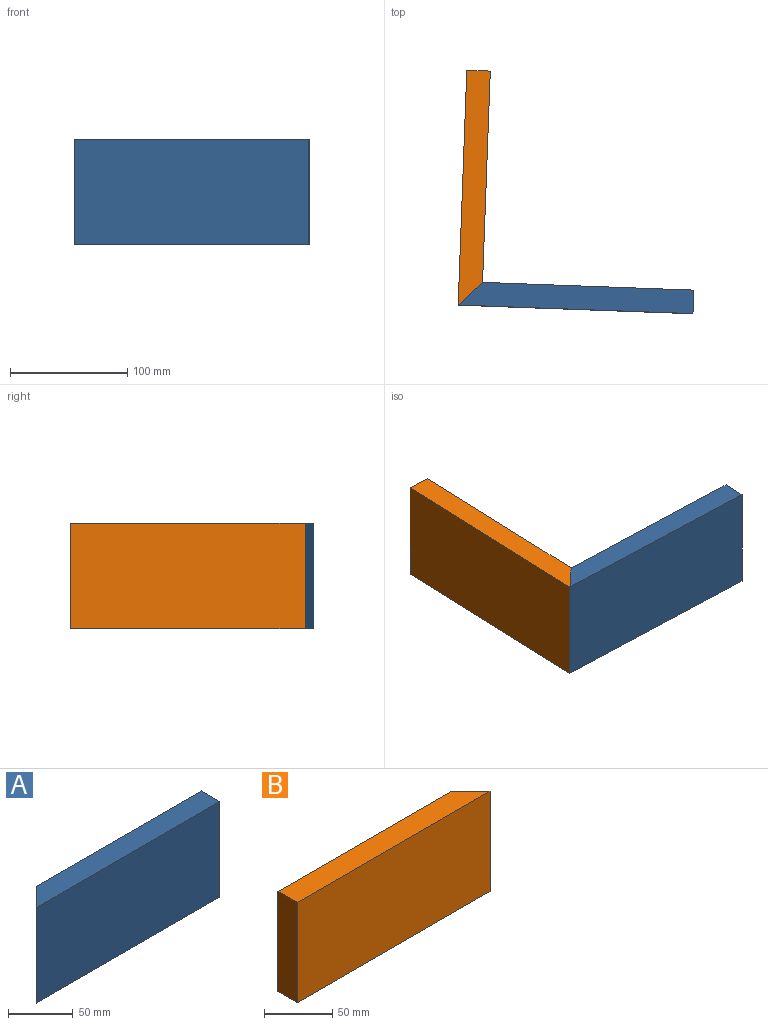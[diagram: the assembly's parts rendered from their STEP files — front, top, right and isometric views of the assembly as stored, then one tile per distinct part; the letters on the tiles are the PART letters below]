
ASSEMBLY  parts=2 mates=1
PART A: 6 faces, bbox 200x20x90 mm
  f0: plane 180x90mm, normal (0,1,0), area 16200mm2, adj f2,f3,f4,f5
  f1: plane 200x90mm, normal (0,-1,0), area 18000mm2, adj f2,f3,f4,f5
  f2: plane 90x20mm, normal (1,0,0), area 1800mm2, adj f0,f1,f3,f4
  f3: plane 200x20mm, normal (0,0,1), area 3800mm2, adj f0,f1,f2,f5
  f4: plane 200x20mm, normal (0,0,-1), area 3800mm2, adj f0,f1,f2,f5
  f5: plane 90x20mm, normal (-0.71,0.71,0), area 2545.6mm2, adj f0,f1,f3,f4
PART B: 6 faces, bbox 200x20x90 mm
  f0: plane 180x90mm, normal (0,1,0), area 16200mm2, adj f1,f3,f4,f5
  f1: plane 90x20mm, normal (-1,0,0), area 1800mm2, adj f0,f2,f3,f4
  f2: plane 200x90mm, normal (0,-1,0), area 18000mm2, adj f1,f3,f4,f5
  f3: plane 200x20mm, normal (0,0,1), area 3800mm2, adj f0,f1,f2,f5
  f4: plane 200x20mm, normal (0,0,-1), area 3800mm2, adj f0,f1,f2,f5
  f5: plane 90x20mm, normal (0.71,0.71,0), area 2545.6mm2, adj f0,f2,f3,f4
PLACE A rot(axis=(0,0,-1),2.1deg) t=(-291.63,53.98,400.62)mm
PLACE B rot(axis=(0,0,-1),92.1deg) t=(-422.26,106.83,400.62)mm
MATE planar A.f5 <-> B.f5  axis (-0.68,0.73,0) through (-392.46,25.41,445.62)mm
